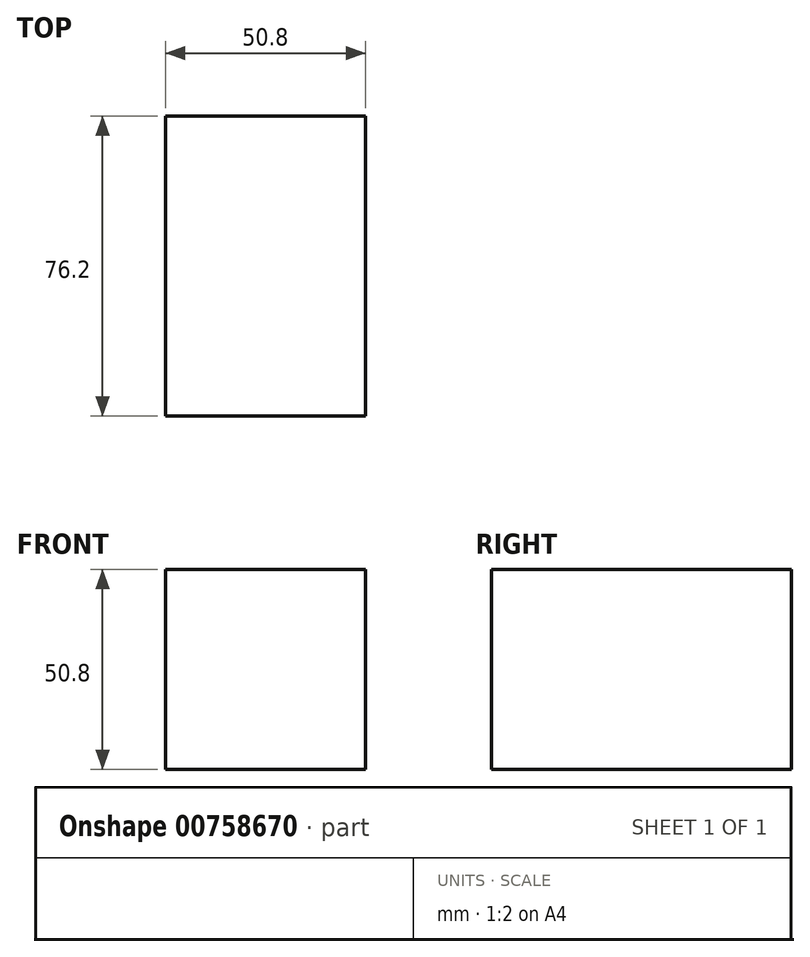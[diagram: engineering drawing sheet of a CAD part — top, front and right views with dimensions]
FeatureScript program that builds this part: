
annotation { "Feature Type Name" : "Feature", "Feature Type Description" : "" }
export const myFeature = defineFeature(function(context is Context, id is Id, definition is map)
    precondition{}
    {
        {
            var Q0;
            Q0=qCreatedBy(makeId("Front.planeOp"),FACE);
            var sketch = newSketch(context, id + "F0", { "sketchPlane" : qUnion([Q0])});
            skLineSegment(sketch, "E0.bottom", {"start": v(25.4, 25.4) * mm, "end": v(-25.4, 25.4) * mm});
            skLineSegment(sketch, "E0.top", {"start": v(25.4, -25.4) * mm, "end": v(-25.4, -25.4) * mm});
            skLineSegment(sketch, "E0.left", {"start": v(25.4, 25.4) * mm, "end": v(25.4, -25.4) * mm});
            skLineSegment(sketch, "E0.right", {"start": v(-25.4, 25.4) * mm, "end": v(-25.4, -25.4) * mm});
            skPoint(sketch, "E0.middle", {"position": v(0, 0) * mm});
            skSolve(sketch);
        }
        {
            var Q0;
            Q0 = qSketchRegion(id + "F0", true);
            extrude(context, id + "F1", {"entities" : qUnion([Q0]), "depth" : 76.2 * mm, "offsetDistance" : 25.4 * mm});
        }
    });
